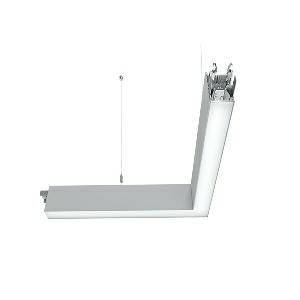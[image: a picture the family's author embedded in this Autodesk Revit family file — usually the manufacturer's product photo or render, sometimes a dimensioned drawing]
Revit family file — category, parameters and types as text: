
# Revit family: idoo_line_-_ilp_3000_840_d_ll_mid_00807704_61de
name_source: partatom
category: Lighting Fixtures
units: mm (PartAtom-declared; Revit-internal decimal feet)

## family parameters
Cut with Voids When Loaded = No
Host = Face
Light Source = No
Part Type = Normal
Room Calculation Point = No
Round Connector Dimension = Use Diameter
Shared = No

## types (1)
- IDOO.line - ILP 3000/840/D/LL MID (1 x LED, 3150 lm, 4000K)
    Apparent Load = 23 VA
    Approval mark = CE
    CIE Flux Codes = 66 91 98 40 100
    Color Rendering = 80-89
    Color Temperature = 4000K
    Control Gear = Electronic ballast
    Default Elevation = 1800 mm
    Description = ILP 3000/840/D|Suspended luminaire|light source: LED|connected load: 220-240 V, 50/60 Hz|Power consumption: approx. 23 W|standby: approx. 0,20|luminous flux: 3150 lm|luminous efficacy: 136 lm/W|light distribution: Direct/indirect|direct ratio: approx. 40 %|colour temperature: Cold white, ca. 4000 K|color rendering index (CRI): >= 80|chromaticity tolerance:  3 SDCM|System of protection: IP 40|technology: Continuously dimmable|luminaire body|material: Sectional aluminium|colour: Silver|lamp cover: Acrylic (PMMA), Clear|Fastening: Steel cable 0.3 - 0.7 m|glare control: Prism aperture|luminance(L65): <= 2700 cd/m|unified glare rating(4H 8H): <=  16|special features: DALI Load 1x, TouchDIM - dimming via standard switch, Through-wired, up to 18 m on one mains connection, Flicker-free, Continous light without dark z, 90░ rerouting on the left side, Suitable as emergency lighting, Mechanical and electrical connection of the individual modules without tools|
    Frequency = 50 Hz
    Height = 110 mm
    Lamp = 1 x LED
    Lamp Light Flux = 3150 lm
    Lamp count = 1
    Length = 600 mm
    Luminous efficacy = 137 lm/W
    Manufacturer = Waldmann
    ModVariant = No
    Model = 00807704
    Mounting Place = Ceiling
    Mounting Type = Pendant
    Number of Poles = 1
    OnlyDefault = Yes
    Power Factor = 1
    Product Name = IDOO.line - ILP 3000/840/D/LL MID
    Product group = Suspended luminaire
    ProductGroupID = 9
    Protection Class = Protection class I
    Protection Degree = IP 40
    RLX_Detail_Level = 1
    RLX_Emergency_Light_Flux = 0 lm
    RLX_Emergency_Type = 0
    RLX_Emergency_Type_DB = No
    RlxData = <blob elided: 21681 chars, md5=a774cbe6>
    Socket = socket
    Standby Power = 0 W
    System Light Flux = 3150 lm
    System Power = 23 W
    Type Comments = Product without accessories
    Type Image = ilp_dlp_ll_si.jpg
    URL = http://relux.com
    VarID = ---
    Voltage = 230 V
    Voltage Range = 220-240 V
    Weight = 0.00 kg
    Width = 600 mm

## geometry (parser evidence)
native form markers: Blend x4, Sweep x14
no freeform markers — native parametric forms only
